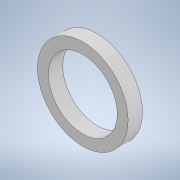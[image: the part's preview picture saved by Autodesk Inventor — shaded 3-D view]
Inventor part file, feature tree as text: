
AUTODESK INVENTOR PART (.ipt)
format: ipt  version: 2020 (Build 240168000, 168)  size: 101,376 bytes
history: native  units: in
note: dims shown in document units (in); Inventor stores cm internally (conversion verified against a paired STEP export)
features: extrude x1, sketch x1
ambient origin geometry x8: Origin, YZ Plane, XZ Plane, XY Plane, X Axis, Y Axis, Z Axis, Center Point
bodies: Solid1 (feature_tree)
feature tree (2):
  extrude  "Extrusion1"  Depth=0.0625in
  sketch  "Sketch1"  dims[d0=0.3in d1=0.0472in d2=0.0625in d3=0.0in]
